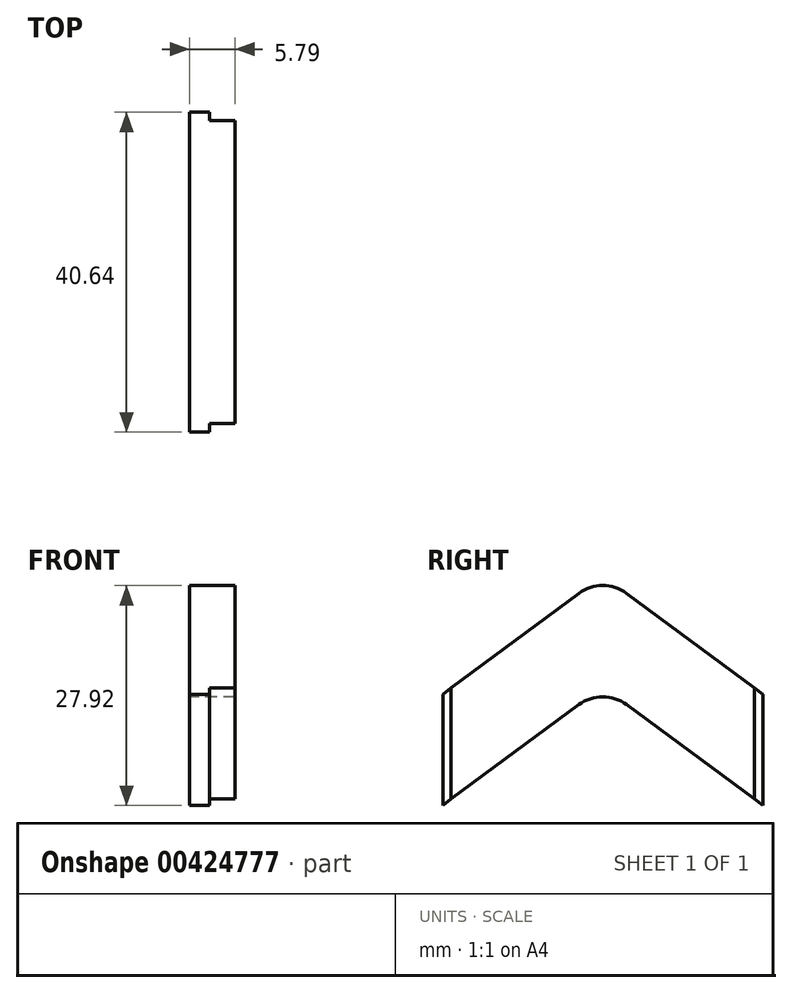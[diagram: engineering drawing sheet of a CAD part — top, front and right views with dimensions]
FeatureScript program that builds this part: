
annotation { "Feature Type Name" : "Feature", "Feature Type Description" : "" }
export const myFeature = defineFeature(function(context is Context, id is Id, definition is map)
    precondition{}
    {
        {
            var Q0;
            Q0=qCreatedBy(makeId("Right.planeOp"),FACE);
            var sketch = newSketch(context, id + "F0", { "sketchPlane" : qUnion([Q0])});
            skArc(sketch, "E0", {"start": v(3.02, 13.13) * mm, "mid": v(1.6, 13.87) * mm, "end": v(0, 14.12) * mm});
            skLineSegment(sketch, "E1", {"start": v(3.02, 13.13) * mm, "end": v(20.32, 0.33) * mm});
            skLineSegment(sketch, "E2", {"start": v(20.32, 0.33) * mm, "end": v(20.32, -13.8) * mm});
            skLineSegment(sketch, "E3", {"start": v(20.32, -13.8) * mm, "end": v(3.02, -1) * mm});
            skArc(sketch, "E4", {"start": v(3.02, -1) * mm, "mid": v(1.6, -0.26) * mm, "end": v(0, 0) * mm});
            skArc(sketch, "E5.MirrorCS", {"start": v(-3.02, -1) * mm, "mid": v(-1.6, -0.26) * mm, "end": v(0, 0) * mm});
            skLineSegment(sketch, "E6.MirrorCS", {"start": v(-20.32, -13.8) * mm, "end": v(-3.02, -1) * mm});
            skLineSegment(sketch, "E7.MirrorCS", {"start": v(-20.32, 0.33) * mm, "end": v(-20.32, -13.8) * mm});
            skLineSegment(sketch, "E8.MirrorCS", {"start": v(-3.02, 13.13) * mm, "end": v(-20.32, 0.33) * mm});
            skArc(sketch, "E9.MirrorCS", {"start": v(-3.02, 13.13) * mm, "mid": v(-1.6, 13.87) * mm, "end": v(0, 14.12) * mm});
            skSolve(sketch);
        }
        {
            var Q0;
            Q0=makeQuery(id+"F0.imprint","IMPRINT",FACE,{"disambiguationData":[TD([[makeQuery(id+"F0.imprint","IMPRINT",EDGE,{"derivedFrom":sQuery(id+"F0.wireOp",EDGE,"E0")}),1.0]])]});
            extrude(context, id + "F1", {"entities" : qUnion([Q0]), "depth" : 5.8 * mm});
        }
        {
            var Q0;
            Q0=makeQuery(id+"F1.opExtrude","CAP_FACE",FACE,{"disambiguationData":[OSD([sQuery(id+"F0.wireOp",EDGE,"E0"),sQuery(id+"F0.wireOp",EDGE,"E1"),sQuery(id+"F0.wireOp",EDGE,"E2"),sQuery(id+"F0.wireOp",EDGE,"E3"),sQuery(id+"F0.wireOp",EDGE,"E4"),sQuery(id+"F0.wireOp",EDGE,"E5.MirrorCS"),sQuery(id+"F0.wireOp",EDGE,"E6.MirrorCS"),sQuery(id+"F0.wireOp",EDGE,"E7.MirrorCS"),sQuery(id+"F0.wireOp",EDGE,"E8.MirrorCS"),sQuery(id+"F0.wireOp",EDGE,"E9.MirrorCS")])],"isStart":false});
            var sketch = newSketch(context, id + "F2", { "sketchPlane" : qUnion([Q0])});
            skLineSegment(sketch, "E10", {"start": v(20.32, -13.8) * mm, "end": v(20.32, 0.33) * mm});
            skLineSegment(sketch, "E11", {"start": v(20.32, 0.33) * mm, "end": v(19.25, 1.12) * mm});
            skLineSegment(sketch, "E12", {"start": v(19.25, 1.12) * mm, "end": v(19.25, -13) * mm});
            skLineSegment(sketch, "E13", {"start": v(19.25, -13) * mm, "end": v(20.32, -13.8) * mm});
            skLineSegment(sketch, "E14.MirrorCS", {"start": v(-19.25, 1.12) * mm, "end": v(-19.25, -13) * mm});
            skLineSegment(sketch, "E15.MirrorCS", {"start": v(-20.32, 0.33) * mm, "end": v(-19.25, 1.12) * mm});
            skLineSegment(sketch, "E16.MirrorCS", {"start": v(-20.32, -13.8) * mm, "end": v(-20.32, 0.33) * mm});
            skLineSegment(sketch, "E17.MirrorCS", {"start": v(-19.25, -13) * mm, "end": v(-20.32, -13.8) * mm});
            skSolve(sketch);
        }
        {
            var Q0;
            Q0 = qSketchRegion(id + "F2", true);
            extrude(context, id + "F3", {"entities" : qUnion([Q0]), "operationType" : NewBodyOperationType.REMOVE, "oppositeDirection" : true, "depth" : 3.25 * mm});
        }
    });
